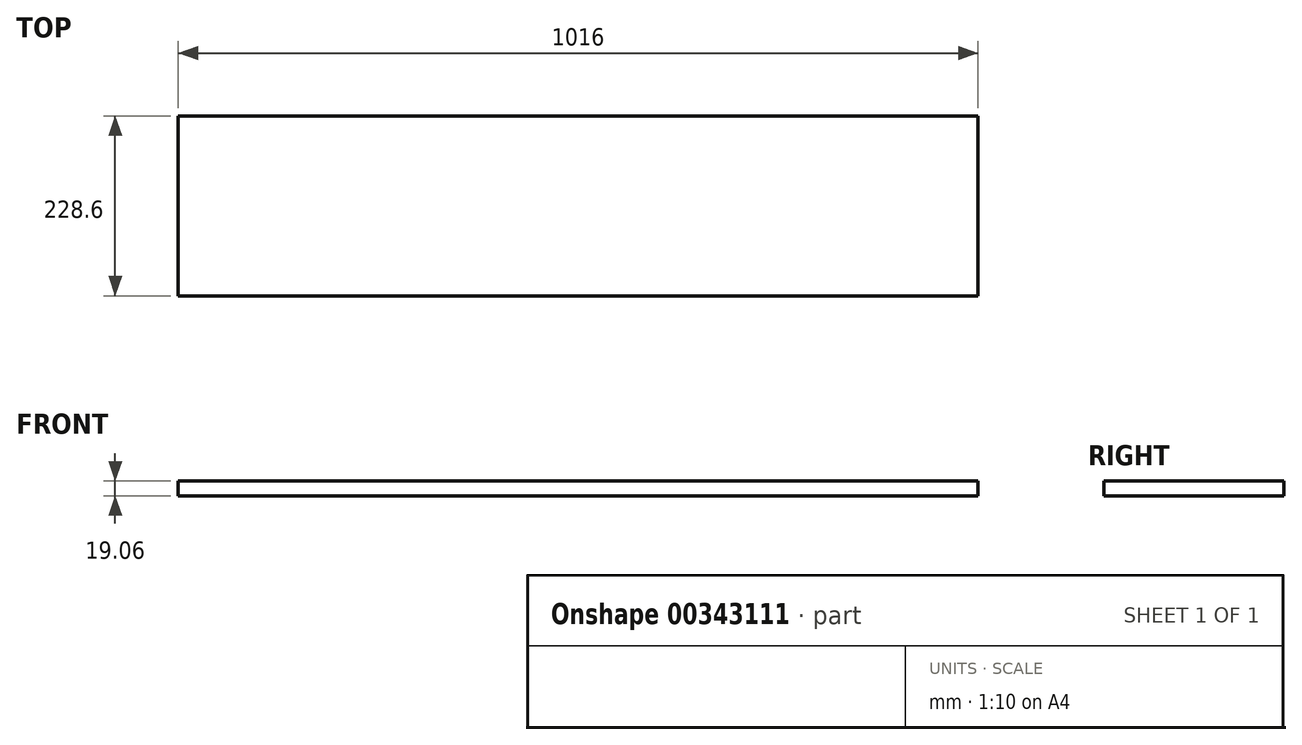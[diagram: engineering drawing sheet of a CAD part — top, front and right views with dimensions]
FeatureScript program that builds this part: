
annotation { "Feature Type Name" : "Feature", "Feature Type Description" : "" }
export const myFeature = defineFeature(function(context is Context, id is Id, definition is map)
    precondition{}
    {
        {
            var Q0;
            Q0=qCreatedBy(makeId("Right.planeOp"),FACE);
            var sketch = newSketch(context, id + "F0", { "sketchPlane" : qUnion([Q0])});
            skLineSegment(sketch, "E0.bottom", {"start": v(-114.3, 9.53) * mm, "end": v(114.3, 9.53) * mm});
            skLineSegment(sketch, "E0.top", {"start": v(-114.3, -9.52) * mm, "end": v(114.3, -9.52) * mm});
            skLineSegment(sketch, "E0.left", {"start": v(-114.3, 9.53) * mm, "end": v(-114.3, -9.52) * mm});
            skLineSegment(sketch, "E0.right", {"start": v(114.3, 9.53) * mm, "end": v(114.3, -9.52) * mm});
            skSolve(sketch);
        }
        {
            var Q0;
            Q0=makeQuery(id+"F0.imprint","IMPRINT",FACE,{"disambiguationData":[TD([[makeQuery(id+"F0.imprint","IMPRINT",EDGE,{"derivedFrom":sQuery(id+"F0.wireOp",EDGE,"E0.bottom")}),-1.0]])]});
            extrude(context, id + "F1", {"entities" : qUnion([Q0]), "endBound" : BoundingType.SYMMETRIC, "depth" : 1016 * mm});
        }
    });
